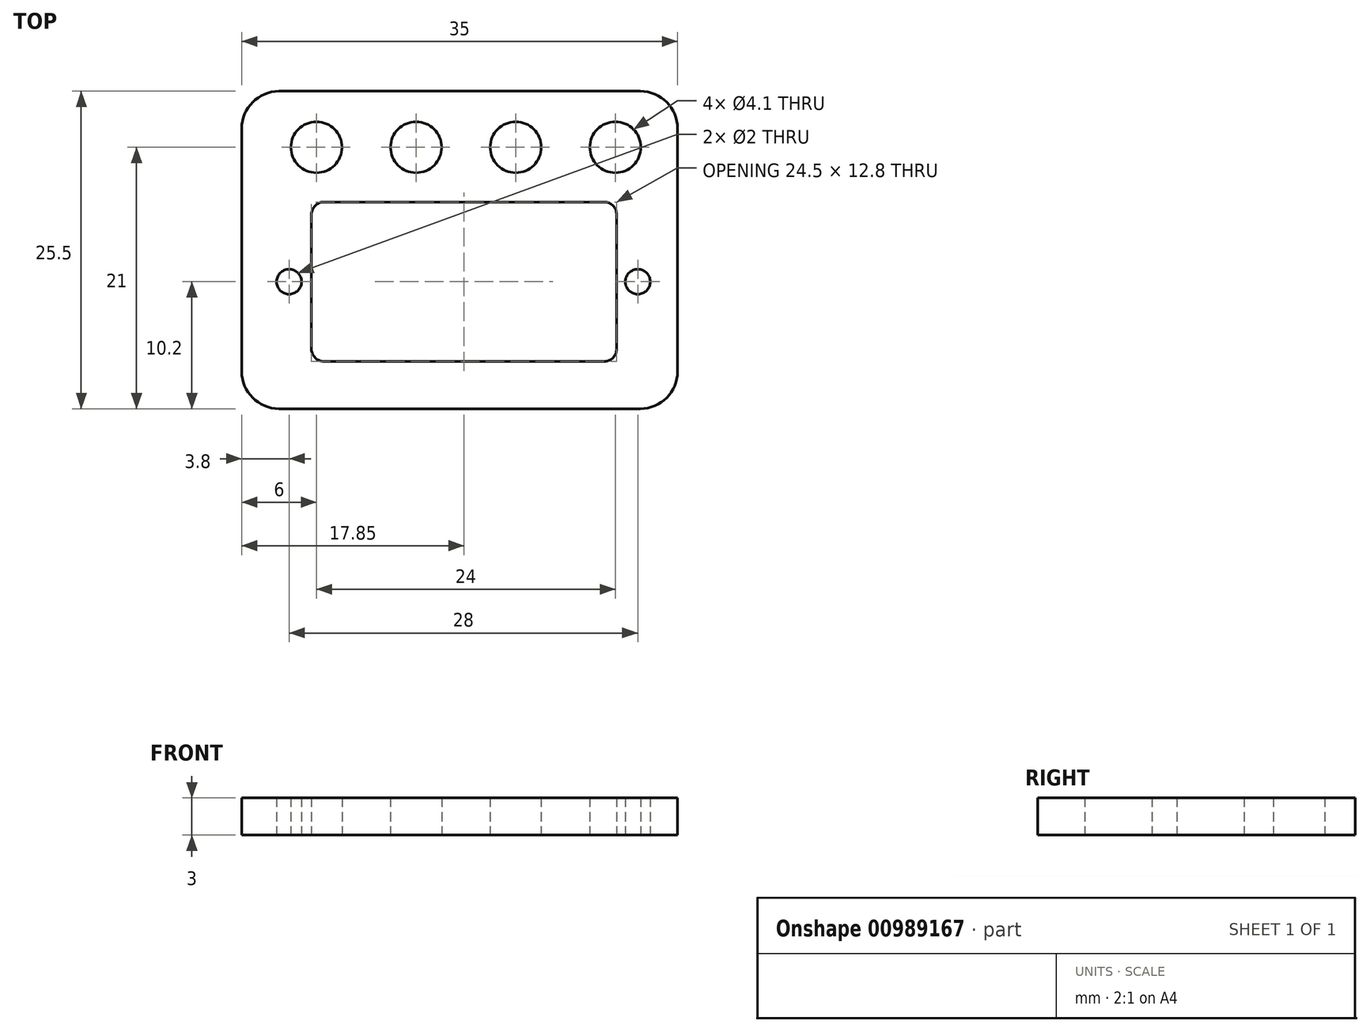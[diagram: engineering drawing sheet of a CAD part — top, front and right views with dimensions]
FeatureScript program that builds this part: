
annotation { "Feature Type Name" : "Feature", "Feature Type Description" : "" }
export const myFeature = defineFeature(function(context is Context, id is Id, definition is map)
    precondition{}
    {
        {
            assignVariable(context, id + "F0", {"name" : "holderZ", "anyValue" : 3});
        }
        {
            var Q0;
            Q0=qCreatedBy(makeId("Top.planeOp"),FACE);
            var sketch = newSketch(context, id + "F1", { "sketchPlane" : qUnion([Q0])});
            skLineSegment(sketch, "E0.bottom", {"start": v(-17.5, 12.75) * mm, "end": v(17.5, 12.75) * mm});
            skLineSegment(sketch, "E0.top", {"start": v(-17.5, -12.75) * mm, "end": v(17.5, -12.75) * mm});
            skLineSegment(sketch, "E0.left", {"start": v(-17.5, 12.75) * mm, "end": v(-17.5, -12.75) * mm});
            skLineSegment(sketch, "E0.right", {"start": v(17.5, 12.75) * mm, "end": v(17.5, -12.75) * mm});
            skLineSegment(sketch, "E1.bottom", {"start": v(-11.9, 3.85) * mm, "end": v(12.6, 3.85) * mm});
            skLineSegment(sketch, "E1.top", {"start": v(-11.9, -8.95) * mm, "end": v(12.6, -8.95) * mm});
            skLineSegment(sketch, "E1.left", {"start": v(-11.9, 3.85) * mm, "end": v(-11.9, -8.95) * mm});
            skLineSegment(sketch, "E1.right", {"start": v(12.6, 3.85) * mm, "end": v(12.6, -8.95) * mm});
            skCircle(sketch, "E2", {"center": v(-11.5, 8.25) * mm, "radius": 2.05 * mm});
            skCircle(sketch, "E3", {"center": v(12.5, 8.25) * mm, "radius": 2.05 * mm});
            skCircle(sketch, "E4", {"center": v(-3.5, 8.25) * mm, "radius": 2.05 * mm});
            skCircle(sketch, "E5", {"center": v(4.5, 8.25) * mm, "radius": 2.05 * mm});
            skCircle(sketch, "E6", {"center": v(-13.7, -2.55) * mm, "radius": 1 * mm});
            skCircle(sketch, "E7", {"center": v(14.3, -2.55) * mm, "radius": 1 * mm});
            skSolve(sketch);
        }
        {
            var Q0;
            Q0=makeQuery(id+"F1.imprint","IMPRINT",FACE,{"disambiguationData":[TD([[makeQuery(id+"F1.imprint","IMPRINT",EDGE,{"derivedFrom":sQuery(id+"F1.wireOp",EDGE,"E0.bottom")}),-1.0]])]});
            extrude(context, id + "F2", {"entities" : qUnion([Q0]), "depth" : getVariable(context, 'holderZ') * mm, "offsetDistance" : 25.4 * mm});
        }
        {
            var Q0;
            Q0=makeQuery(id+"F2.opExtrude","SWEPT_EDGE",EDGE,{"disambiguationData":[OSD([sQuery(id+"F1.wireOp",EDGE,"E0.bottom"),sQuery(id+"F1.wireOp",EDGE,"E0.left")])]});
            var Q1;
            Q1=makeQuery(id+"F2.opExtrude","SWEPT_EDGE",EDGE,{"disambiguationData":[OSD([sQuery(id+"F1.wireOp",EDGE,"E0.bottom"),sQuery(id+"F1.wireOp",EDGE,"E0.right")])]});
            var Q2;
            Q2=makeQuery(id+"F2.opExtrude","SWEPT_EDGE",EDGE,{"disambiguationData":[OSD([sQuery(id+"F1.wireOp",EDGE,"E0.top"),sQuery(id+"F1.wireOp",EDGE,"E0.right")])]});
            var Q3;
            Q3=makeQuery(id+"F2.opExtrude","SWEPT_EDGE",EDGE,{"disambiguationData":[OSD([sQuery(id+"F1.wireOp",EDGE,"E0.top"),sQuery(id+"F1.wireOp",EDGE,"E0.left")])]});
            fillet(context, id + "F3", {"entities" : qUnion([Q0, Q1, Q2, Q3]), "radius" : 3 * mm, "tangentPropagation" : true, "allowEdgeOverflow" : false});
        }
        {
            var Q0;
            Q0=makeQuery(id+"F2.opExtrude","SWEPT_EDGE",EDGE,{"disambiguationData":[OSD([sQuery(id+"F1.wireOp",EDGE,"E1.bottom"),sQuery(id+"F1.wireOp",EDGE,"E1.left")])]});
            var Q1;
            Q1=makeQuery(id+"F2.opExtrude","SWEPT_EDGE",EDGE,{"disambiguationData":[OSD([sQuery(id+"F1.wireOp",EDGE,"E1.bottom"),sQuery(id+"F1.wireOp",EDGE,"E1.right")])]});
            var Q2;
            Q2=makeQuery(id+"F2.opExtrude","SWEPT_EDGE",EDGE,{"disambiguationData":[OSD([sQuery(id+"F1.wireOp",EDGE,"E1.top"),sQuery(id+"F1.wireOp",EDGE,"E1.right")])]});
            var Q3;
            Q3=makeQuery(id+"F2.opExtrude","SWEPT_EDGE",EDGE,{"disambiguationData":[OSD([sQuery(id+"F1.wireOp",EDGE,"E1.top"),sQuery(id+"F1.wireOp",EDGE,"E1.left")])]});
            fillet(context, id + "F4", {"entities" : qUnion([Q0, Q1, Q2, Q3]), "radius" : 1 * mm, "tangentPropagation" : true, "allowEdgeOverflow" : false});
        }
    });
